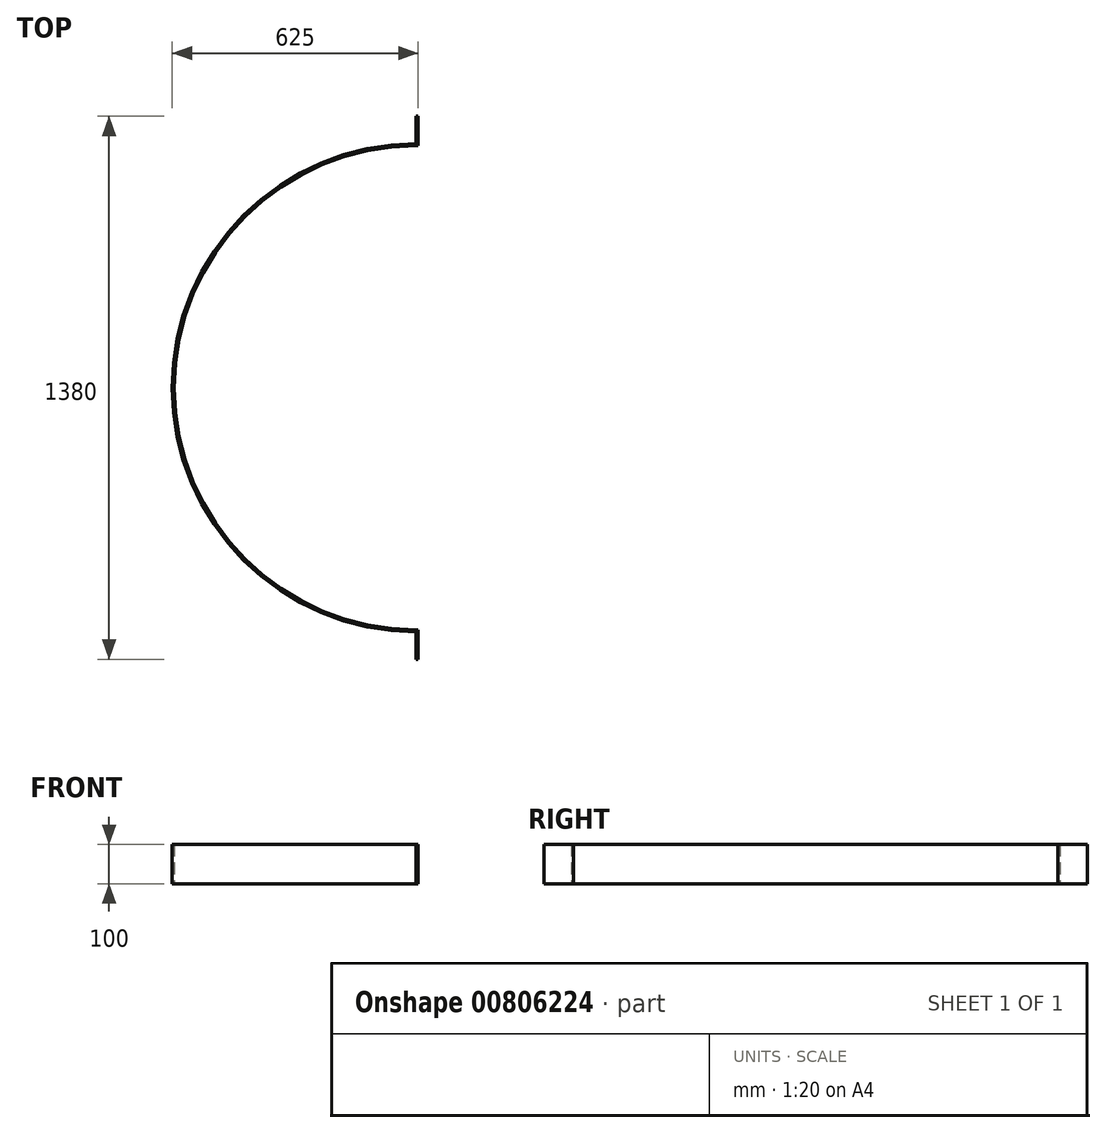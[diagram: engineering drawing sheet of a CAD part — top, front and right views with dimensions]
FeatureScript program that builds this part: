
annotation { "Feature Type Name" : "Feature", "Feature Type Description" : "" }
export const myFeature = defineFeature(function(context is Context, id is Id, definition is map)
    precondition{}
    {
        {
            var Q0;
            Q0=qCreatedBy(makeId("Top.planeOp"),FACE);
            var sketch = newSketch(context, id + "F0", { "sketchPlane" : qUnion([Q0])});
            skArc(sketch, "E0", {"start": v(-620, 0) * mm, "mid": v(-438.4, -438.4) * mm, "end": v(0, -620) * mm});
            skLineSegment(sketch, "E1", {"start": v(0, 0) * mm, "end": v(0, -620) * mm, "construction": true});
            skLineSegment(sketch, "E2", {"start": v(0, 0) * mm, "end": v(-620, 0) * mm, "construction": true});
            skArc(sketch, "E3.0", {"start": v(-615, 0) * mm, "mid": v(-434.87, -434.87) * mm, "end": v(0, -615) * mm});
            skLineSegment(sketch, "E4", {"start": v(0, -615) * mm, "end": v(0, -690) * mm});
            skLineSegment(sketch, "E5", {"start": v(0, -690) * mm, "end": v(5, -690) * mm});
            skLineSegment(sketch, "E6", {"start": v(5, -690) * mm, "end": v(5, -615) * mm});
            skLineSegment(sketch, "E7", {"start": v(5, -615) * mm, "end": v(0, -615) * mm});
            skLineSegment(sketch, "E8", {"start": v(-615, 0) * mm, "end": v(-620, 0) * mm});
            skSolve(sketch);
        }
        {
            var Q0;
            Q0=qSketchRegion(id+"F0",true);
            extrude(context, id + "F1", {"entities" : qUnion([Q0]), "depth" : 100 * mm, "offsetDistance" : 25 * mm});
        }
        {
            var Q0;
            Q0=makeQuery(id+"F1.opExtrude","SWEPT_BODY",BODY,{"disambiguationData":[OSD([sQuery(id+"F0.wireOp",EDGE,"E0"),sQuery(id+"F0.wireOp",EDGE,"E3.0"),sQuery(id+"F0.wireOp",EDGE,"E4"),sQuery(id+"F0.wireOp",EDGE,"E5"),sQuery(id+"F0.wireOp",EDGE,"E6"),sQuery(id+"F0.wireOp",EDGE,"E7"),sQuery(id+"F0.wireOp",EDGE,"E8")])]});
            var Q1;
            Q1=makeQuery(id+"F1.opExtrude","SWEPT_FACE",FACE,{"disambiguationData":[OSD([sQuery(id+"F0.wireOp",EDGE,"E8")])]});
            mirror(context, id + "F2", {"operationType" : NewBodyOperationType.ADD, "entities" : qUnion([Q0]), "mirrorPlane" : qUnion([Q1])});
        }
    });
